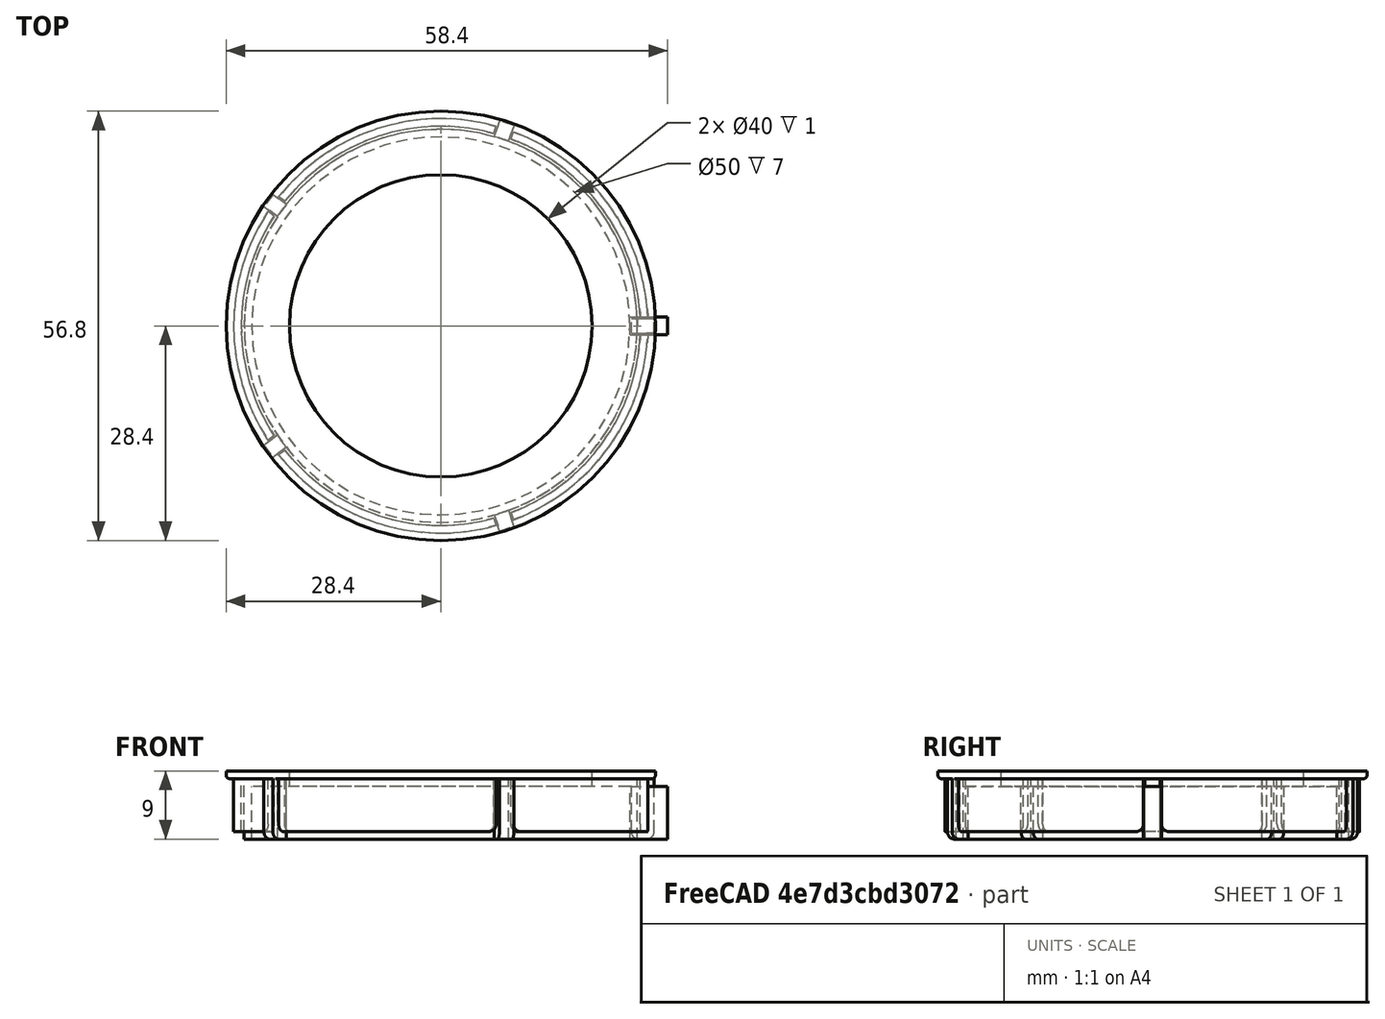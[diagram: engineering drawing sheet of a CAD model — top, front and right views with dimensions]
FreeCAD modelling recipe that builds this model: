
FCSTD DOCUMENT  (FreeCAD 0.20R29410 (Git))
Label: illuminator_ext
License: All rights reserved
LicenseURL: http://en.wikipedia.org/wiki/All_rights_reserved
objects: Part::Cylinder×7, Part::MultiFuse×4, Part::Fillet×3, Part::Box×2, Part::FeaturePython×2, Part::Cut×2
note: 18 computed .brp shape members not serialized (recipe doc carries the construction recipe); baked Part::Feature solids carry a one-line shape summary decoded from their .brp

FEATURE [Part::Cylinder] Cylinder  label="extract cylinder"
  Angle = 360
  AttacherType = Attacher::AttachEngine3D
  FirstAngle = 0
  Height = 7
  Radius = 25
  SecondAngle = 0
FEATURE [Part::Cylinder] Cylinder001  label="outer cylinder"
  Angle = 360
  AttacherType = Attacher::AttachEngine3D
  FirstAngle = 0
  Height = 8
  Radius = 26
  SecondAngle = 0
  expr: Height = <<extract cylinder>>.Height + 1mm
  expr: Radius = <<extract cylinder>>.Radius + 1mm
FEATURE [Part::Cylinder] Cylinder002  label="lens hole"
  Angle = 360
  AttacherType = Attacher::AttachEngine3D
  FirstAngle = 0
  Height = 20
  Radius = 20
  SecondAngle = 0
FEATURE [Part::MultiFuse] Fusion  label="extract fusion"
  Shapes = -> [Cylinder,Cylinder002]
FEATURE [Part::Cylinder] Cylinder003  label="extract cylinder001"
  Angle = 360
  AttacherType = Attacher::AttachEngine3D
  FirstAngle = 0
  Height = 7
  Radius = 26.4
  SecondAngle = 0
  expr: Height = <<outer cylinder>>.Height - 1mm
  expr: Radius = <<outer cylinder>>.Radius + 0.4mm
FEATURE [Part::Cylinder] Cylinder004  label="outer cylinder001"
  Angle = 360
  AttacherType = Attacher::AttachEngine3D
  FirstAngle = 0
  Height = 8
  Radius = 27.4
  SecondAngle = 0
  expr: Height = <<outer cylinder>>.Height
  expr: Radius = <<extract cylinder001>>.Radius + 1mm
FEATURE [Part::Cylinder] Cylinder005  label="lens hole001"
  Angle = 360
  AttacherType = Attacher::AttachEngine3D
  FirstAngle = 0
  Height = 20
  Radius = 20
  SecondAngle = 0
FEATURE [Part::Box] Box  label="tick cube"
  AttacherType = Attacher::AttachEngine3D
  Height = 8
  Length = 3
  Placement = pos=(25.2,-1,0) rot=(0,0,1;0rad)
  Width = 2
  expr: .Placement.Base.x = <<extract cylinder>>.Radius + 0.2mm
  expr: .Placement.Base.y = -Width / 2
  expr: Height = <<outer cylinder>>.Height
FEATURE [Part::Fillet] Fillet  label="tick fillet"
  Base = -> Box
  Edges = 2 edges r=1: [Edge4,Edge8]
FEATURE [Part::FeaturePython] Array  label="tick array"  # Draft array (typed FeaturePython)
  AlwaysSyncPlacement = false
  Angle = 360
  ArrayType = 1
  Axis = (0,0,1)
  Base = -> Fillet
  Center = (0,0,0)
  Count = 5
  ExpandArray = false
  Fuse = false
  IntervalAxis = (0,0,0)
  IntervalX = (50,0,0)
  IntervalY = (0,50,0)
  IntervalZ = (0,0,50)
  NumberCircles = 3
  NumberPolar = 5
  NumberX = 2
  NumberY = 2
  NumberZ = 1
  PlacementList = 5 placements: [(0,0,0),(0,0,0),(0,0,0),(0,0,0),(0,0,0)]
  RadialDistance = 50
  ScaleList = (5) [(1,1,1),(1,1,1),(1,1,1),(1,1,1),(1,1,1)]
  Symmetry = 1
  TangentialDistance = 25
FEATURE [Part::MultiFuse] Fusion002  label="body fusion"
  Shapes = -> [Cylinder001,Array]
FEATURE [Part::Cut] Cut  label="border cut"
  Base = -> Fusion002
  Tool = -> Fusion
FEATURE [Part::Box] Box001  label="tick cube001"
  AttacherType = Attacher::AttachEngine3D
  Height = 7
  Length = 5
  Placement = pos=(25,-1.2,0) rot=(0,0,1;0rad)
  Width = 2.4
  expr: .Placement.Base.x = <<extract cylinder>>.Radius
  expr: .Placement.Base.y = -Width / 2
  expr: Height = <<extract cylinder001>>.Height
  expr: Width = <<tick cube>>.Width + 0.4mm
FEATURE [Part::FeaturePython] Array001  label="tick array001"  # Draft array (typed FeaturePython)
  AlwaysSyncPlacement = false
  Angle = 360
  ArrayType = 1
  Axis = (0,0,1)
  Base = -> Box001
  Center = (0,0,0)
  Count = 5
  ExpandArray = false
  Fuse = false
  IntervalAxis = (0,0,0)
  IntervalX = (50,0,0)
  IntervalY = (0,50,0)
  IntervalZ = (0,0,50)
  NumberCircles = 3
  NumberPolar = 5
  NumberX = 2
  NumberY = 2
  NumberZ = 1
  PlacementList = 5 placements: [(25,-1.2,0),(8.86669,23.4056,0),(-19.5201,15.6655,0),(-20.9308,-13.7238,0),(6.58416,-24.1472,0)]
  RadialDistance = 50
  ScaleList = (5) [(1,1,1),(1,1,1),(1,1,1),(1,1,1),(1,1,1)]
  Symmetry = 1
  TangentialDistance = 25
FEATURE [Part::MultiFuse] Fusion001  label="extract fusion001"
  Shapes = -> [Cylinder003,Cylinder005,Array001]
FEATURE [Part::Cylinder] Cylinder006  label="disk"
  Angle = 360
  AttacherType = Attacher::AttachEngine3D
  FirstAngle = 0
  Height = 1
  Placement = pos=(0,0,7) rot=(0,0,1;0rad)
  Radius = 28.4
  SecondAngle = 0
  expr: .Placement.Base.z = <<extract cylinder001>>.Height
  expr: Radius = <<outer cylinder001>>.Radius + 1mm
FEATURE [Part::Fillet] Fillet001  label="disk fillet"
  Base = -> Cylinder006
  Edges = 1 edges r=0.5: [Edge3]
FEATURE [Part::MultiFuse] Fusion003  label="body fusion001"
  Shapes = -> [Cylinder004,Fillet001]
FEATURE [Part::Cut] Cut001  label="cover cut"
  Base = -> Fusion003
  Placement = pos=(0,0,1) rot=(0,0,1;0rad)
  Tool = -> Fusion001
FEATURE [Part::Fillet] Fillet002  label="cover fillet"
  Base = -> Cut001
  Edges = 10 edges r=1: [Edge84,Edge87,Edge91,Edge94,Edge98,Edge100,Edge105,Edge107,Edge112,Edge114]
